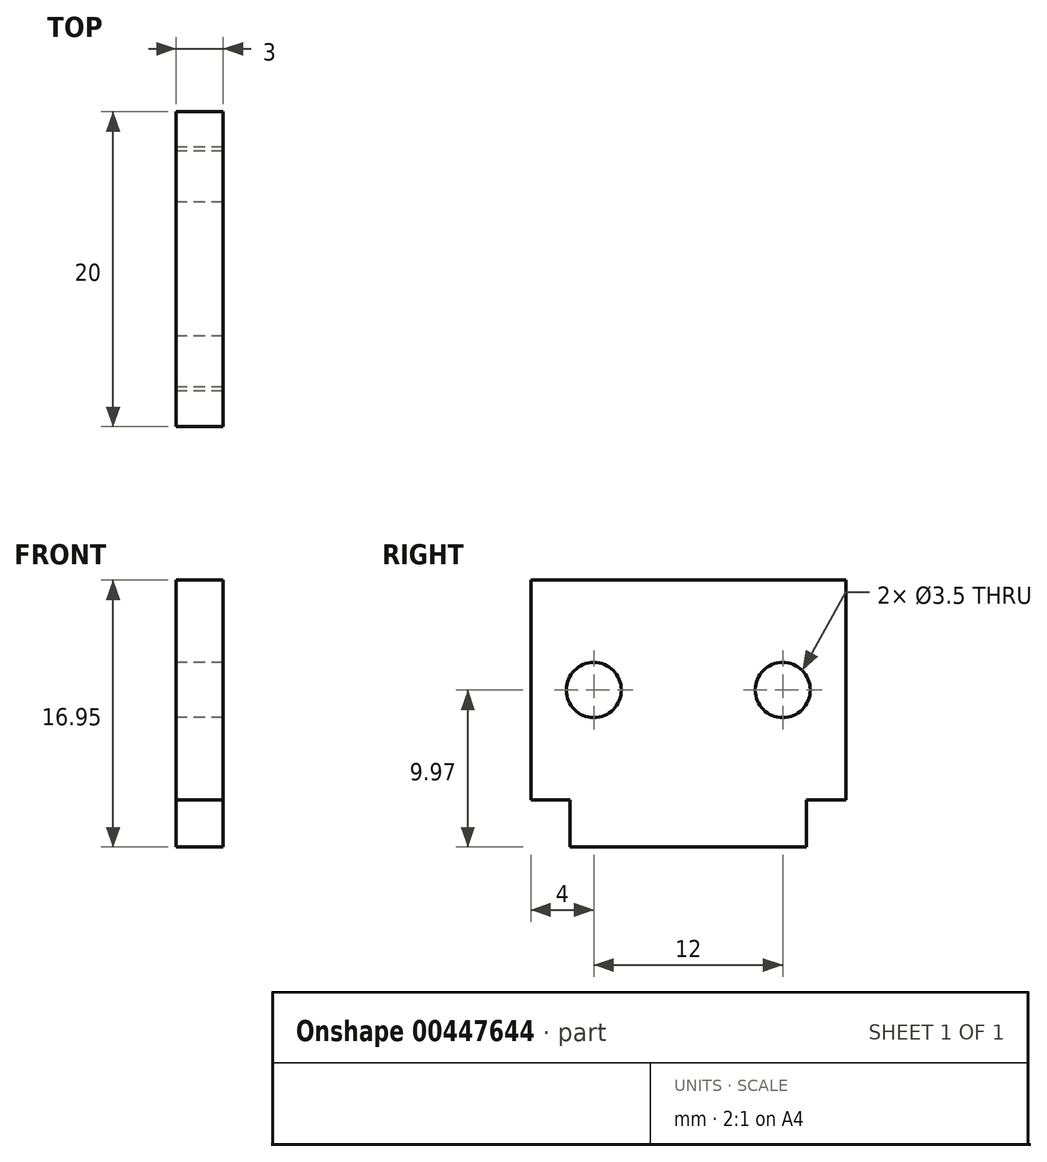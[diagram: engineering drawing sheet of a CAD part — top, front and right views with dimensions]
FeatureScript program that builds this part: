
annotation { "Feature Type Name" : "Feature", "Feature Type Description" : "" }
export const myFeature = defineFeature(function(context is Context, id is Id, definition is map)
    precondition{}
    {
        {
            var Q0;
            Q0=qCreatedBy(makeId("Right.planeOp"),FACE);
            var sketch = newSketch(context, id + "F0", { "sketchPlane" : qUnion([Q0])});
            skLineSegment(sketch, "E0.bottom", {"start": v(10, -6.97) * mm, "end": v(-10, -6.98) * mm});
            skLineSegment(sketch, "E0.top", {"start": v(10, 6.98) * mm, "end": v(-10, 6.97) * mm});
            skLineSegment(sketch, "E0.left", {"start": v(10, -6.98) * mm, "end": v(10, 6.97) * mm});
            skLineSegment(sketch, "E0.right", {"start": v(-10, -6.98) * mm, "end": v(-10, 6.97) * mm});
            skPoint(sketch, "E0.middle", {"position": v(0, 0) * mm});
            skLineSegment(sketch, "E1.bottom", {"start": v(7.5, -9.97) * mm, "end": v(-7.5, -9.98) * mm});
            skLineSegment(sketch, "E1.top", {"start": v(7.5, -6.97) * mm, "end": v(-7.5, -6.98) * mm});
            skLineSegment(sketch, "E1.left", {"start": v(7.5, -9.97) * mm, "end": v(7.5, -6.97) * mm});
            skLineSegment(sketch, "E1.right", {"start": v(-7.5, -9.97) * mm, "end": v(-7.5, -6.97) * mm});
            skPoint(sketch, "E1.middle", {"position": v(0, -8.47) * mm});
            skLineSegment(sketch, "E2.bottom", {"start": v(5, 6.97) * mm, "end": v(-5, 6.97) * mm});
            skLineSegment(sketch, "E2.top", {"start": v(5, 10.02) * mm, "end": v(-5, 10.02) * mm});
            skLineSegment(sketch, "E2.left", {"start": v(5, 6.97) * mm, "end": v(5, 10.02) * mm});
            skLineSegment(sketch, "E2.right", {"start": v(-5, 6.97) * mm, "end": v(-5, 10.02) * mm});
            skPoint(sketch, "E2.middle", {"position": v(0, 8.5) * mm});
            skCircle(sketch, "E3", {"center": v(6, 0) * mm, "radius": 1.75 * mm});
            skCircle(sketch, "E4", {"center": v(-6, 0) * mm, "radius": 1.75 * mm});
            skSolve(sketch);
        }
        {
            var Q0;
            Q0=makeQuery(id+"F0.imprint","IMPRINT",FACE,{"disambiguationData":[TD([[makeQuery(id+"F0.imprint","IMPRINT",EDGE,{"derivedFrom":sQuery(id+"F0.wireOp",EDGE,"RxRQknv1-wJnE-53Rh-R5Zs-tONe4iIZOmeT.bottom")}),-1.0]])]});
            var Q1;
            Q1=makeQuery(id+"F0.imprint","IMPRINT",FACE,{"disambiguationData":[TD([[makeQuery(id+"F0.imprint","IMPRINT",EDGE,{"derivedFrom":sQuery(id+"F0.wireOp",EDGE,"rebLLzOc-MMFz-VvsI-Ydd9-l2fTW7hARkIk.bottom")}),-1.0]])]});
            var Q2;
            Q2=makeQuery(id+"F0.imprint","IMPRINT",FACE,{"disambiguationData":[TD([[makeQuery(id+"F0.imprint","IMPRINT",EDGE,{"derivedFrom":sQuery(id+"F0.wireOp",EDGE,"E1.bottom")}),-1.0]])]});
            var Q3;
            {var subQ4=sQuery(id+"F0.wireOp",EDGE,"E0.left");Q3=makeQuery(id+"F0.imprint","IMPRINT",FACE,{"disambiguationData":[TD([[makeQuery(id+"F0.imprint","IMPRINT",EDGE,{"derivedFrom":subQ4}),1.0]])]});}
            var Q4;
            Q4=makeQuery(id+"F0.imprint","IMPRINT",FACE,{"disambiguationData":[TD([[makeQuery(id+"F0.imprint","IMPRINT",EDGE,{"derivedFrom":sQuery(id+"F0.wireOp",EDGE,"E2.bottom")}),-1.0]])]});
            extrude(context, id + "F1", {"entities" : qUnion([Q0, Q1, Q2, Q3, Q4]), "depth" : 3 * mm});
        }
    });
